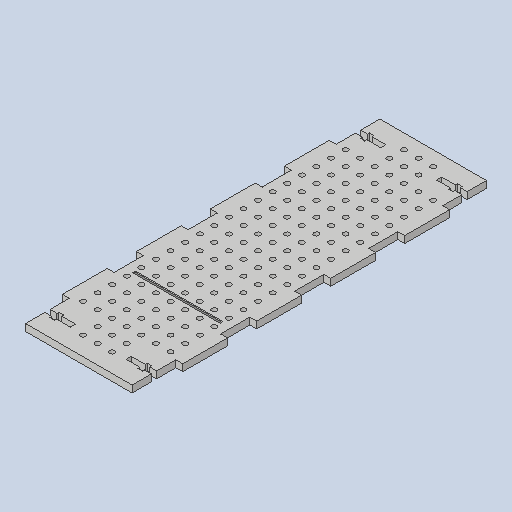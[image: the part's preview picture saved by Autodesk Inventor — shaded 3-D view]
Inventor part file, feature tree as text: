
AUTODESK INVENTOR PART (.ipt)
format: ipt  version: 2022.1 (Build 261234020, 234B)  size: 422,912 bytes
history: native  units: in
note: dims shown in document units (in); Inventor stores cm internally (conversion verified against a paired STEP export)
features: sketch x9, extrude x6, hole x3, pattern_linear x3, reference x2, other x2, projected_geometry x1
ambient origin geometry x8: Origin, YZ Plane, XZ Plane, XY Plane, X Axis, Y Axis, Z Axis, Center Point
bodies: Solid1 (feature_tree)
feature tree (26):
  extrude  "Base"  Depth=12.142in
  hole  "Board Hole"  [1 undecoded]
  pattern_linear  "Patterned Board Holes"  Count1=19 Spacing1=0.5in
  extrude  "Extrusion4"  Depth=1.0in TaperAngle=0.0deg
  sketch  "Sketch13"  dims[d37=0.1772in d38=0.315in d39=0.175in d40=0.25in d41=0.5635in d42=0.465in d43=0.8108in d44=7.4803in d46=0.5in]
  hole  "Hole9"  [1 undecoded]
  extrude  "Extrusion6"  Depth=1.5in
  extrude  "Extrusion7"  Depth=0.2362in
  extrude  "Extrusion8"  Depth=1.5in
  pattern_linear  "Rectangular Pattern6"  Spacing1=1.0in  [1 undecoded]
  sketch  "Sketch19"  dims[d176=0.2362in d177=0.2362in]
  extrude  "Extrusion10"  Depth=0.2362in
  hole  "Hole10"  [1 undecoded]
  pattern_linear  "Rectangular Pattern8"  Spacing1=0.2362in  [1 undecoded]
  sketch  "Sketch1"  dims[d0=4.1224in d1=12.142in]
  sketch  "Sketch7"  dims[d2=0.2362in d3=0.0in d35=1.5in]
  projected_geometry  "Projected Loop1"
  sketch  "Sketch12"  dims[d36=2.0612in]
  sketch  "Sketch16"  dims[d47=2.7559in d49=0.5in d97=1.0in d98=0.0in]
  sketch  "Sketch17"  dims[d132=0.1772in d133=0.75in d134=0.375in d135=0.25in d136=0.5635in d137=1.0in d138=0.8108in d154=1.0in d155=0.0in]
  sketch  "Sketch18"  dims[d163=0.5in d175=1.5in]
  sketch  "Sketch20"  dims[d178=0.2362in d179=1.5in d180=1.0in d181=0.0in d188=0.2362in d189=1.5in d190=0.2362in d191=1.5in d193=0.2362in d194=1.0in d195=0.2362in d196=1.0in d197=0.2362in d198=1.0in d199=0.2362in d200=0.2362in d201=0.2362in d202=1.5355in d203=1.5355in d204=1.5355in d205=1.5355in d206=1.0in d207=1.0in d208=1.0in d217=1.0in d218=0.0in d219=0.7874in d221=0.5in d222=1.1811in d224=0.5in d225=0.128in d234=0.1in d235=0.0394in d236=0.0in d237=1.1024in d238=0.1575in d239=0.315in d240=0.4724in d242=0.6615in d243=0.1772in d244=0.2362in d245=0.3701in d246=0.0787in d247=90.0deg d248=0.315in d249=0.8108in d250=1.1811in d252=0.5in d253=0.7874in d255=0.5in]
  reference  "Reference1"
  reference  "Reference2"
  other  "Baseplate - Metric Holes.iam"
  other  "V3 Mounting Wall:1"
note: 5 required parameter values undecoded (feature->parameter linkage not recoverable at this tier; creation-order binding heuristic only, values carry confidence <= 0.55)
